# Revit family: Shower-Showerhead-KOHLER-Contemporary-K-13688
name_source: partatom
category: Plumbing Fixtures
revit_build: Autodesk Revit 2015 (Build: 20140606_1530(x64)
units: mm (PartAtom-declared; Revit-internal decimal feet)

## types (15) — shared parameters
ADA Compliant = No
Assembly Code = D2010700
CW Connection = No
Date Modified = 12/18/2018
Default Elevation = 0"
Drain Included = No
HW Connection = Yes
Height = 2 3/4"
Length = 8"
Manufacturer = KOHLER Co.
MasterFormat 1995 = 15410
MasterFormat 2004 = 22.41.23
Material = Solid Brass Construction
Panel Thickness = 0"
Pressure = 80.00 psi
Product Documentation Link = http://www.us.kohler.com
Product Name = Contemporary
Product Page URL = http://www.us.kohler.com
Tempered Water Inlet = Tempered Water Inlet
URL = https://www.us.kohler.com
Vent Connection = No
Waste Connection = No
Waste Water Outlet = Waste Water Outlet
Width = 8"

## per-type parameters (varying)
| type | Description | Finish | Flow Rate | Model | Type |
| 2.5 GPM, CP-Polished Chrome | 8 inch Contemporary Round 2.5 gpm rainhead with Katalyst(r) air-induction technology | Kohler-Metal-CP-Polished_Chrome | 3 GPM | K-13688-CP | 1 |
| 2.5 GPM, SN-Vibrant Polished Nicke | 8 inch Contemporary Round 2.5 gpm rainhead with Katalyst(r) air-induction technology | Kohler-Metal-SN-Vibrant_Polished_Nickel | 3 GPM | K-13688-SN | 2 |
| 2.5 GPM, BGD-Vibrant Moderne Brushed Gold | 8 inch Contemporary Round 2.5 gpm rainhead with Katalyst(r) air-induction technology | Kohler-Metal-BGD-Vibrant_Moderne_Brushed_Gold | 3 GPM | K-13688-BGD | 3 |
| 2.5 GPM, BN-Vibrant Brushed Nickel | 8 inch Contemporary Round 2.5 gpm rainhead with Katalyst(r) air-induction technology | Kohler-Metal-BN-Vibrant_Brushed_Nickel | 3 GPM | K-13688-BN | 4 |
| 2.5 GPM, BV-Vibrant Brushed Bronze | 8 inch Contemporary Round 2.5 gpm rainhead with Katalyst(r) air-induction technology | Kohler-Metal-BV-Brushed_Bronze | 3 GPM | K-13688-BV | 5 |
| 2.5 GPM, BL-Matte Black | 8 inch Contemporary Round 2.5 gpm rainhead with Katalyst(r) air-induction technology | Kohler-Metal-BL-Matte_Black | 3 GPM | K-13688-BL | 6 |
| 2.5 GPM, RGD-Vibrant Rose Gold | 8 inch Contemporary Round 2.5 gpm rainhead with Katalyst(r) air-induction technology | Kohler-Metal-RGD-Polished_Rose_Gold | 3 GPM | K-13688-RGD | 7 |
| 2.5 GPM, TT-Titanium | 8 inch Contemporary Round 2.5 gpm rainhead with Katalyst(r) air-induction technology | Kohler-Metal-TT-Vibrant_Titanium | 3 GPM | K-13688-TT | 8 |
| 1.75 GPM, BGD-Vibrant Moderne Brushed Gold | 8 inch Contemporary Round 1.75 gpm rainhead with Katalyst® air-induction technology | Kohler-Metal-BGD-Vibrant_Moderne_Brushed_Gold | 2 GPM | K-13688-G-BGD | 11 |
| 1.75 GPM, CP-Polished Chrome | 8 inch Contemporary Round 1.75 gpm rainhead with Katalyst® air-induction technology | Kohler-Metal-CP-Polished_Chrome | 2 GPM | K-13688-G-CP | 9 |
| 1.75 GPM, SN-Vibrant Polished Nicke | 8 inch Contemporary Round 1.75 gpm rainhead with Katalyst® air-induction technology | Kohler-Metal-SN-Vibrant_Polished_Nickel | 2 GPM | K-13688-G-SN | 10 |
| 1.75 GPM, BN-Vibrant Brushed Nickel | 8 inch Contemporary Round 1.75 gpm rainhead with Katalyst® air-induction technology | Kohler-Metal-BN-Vibrant_Brushed_Nickel | 2 GPM | K-13688-G-BN | 12 |
| 1.75 GPM, BV-Vibrant Brushed Bronze | 8 inch Contemporary Round 1.75 gpm rainhead with Katalyst® air-induction technology | Kohler-Metal-BV-Brushed_Bronze | 2 GPM | K-13688-G-BV | 13 |
| 1.75 GPM, BL-Matte Black | 8 inch Contemporary Round 1.75 gpm rainhead with Katalyst® air-induction technology | Kohler-Metal-BL-Matte_Black | 2 GPM | K-13688-G-BL | 14 |
| 1.75 GPM, TT-Titanium | 8 inch Contemporary Round 1.75 gpm rainhead with Katalyst® air-induction technology | Kohler-Metal-TT-Vibrant_Titanium | 2 GPM | K-13688-G-TT | 15 |

## geometry (parser evidence)
native form markers: Sweep x5
no freeform markers — native parametric forms only
